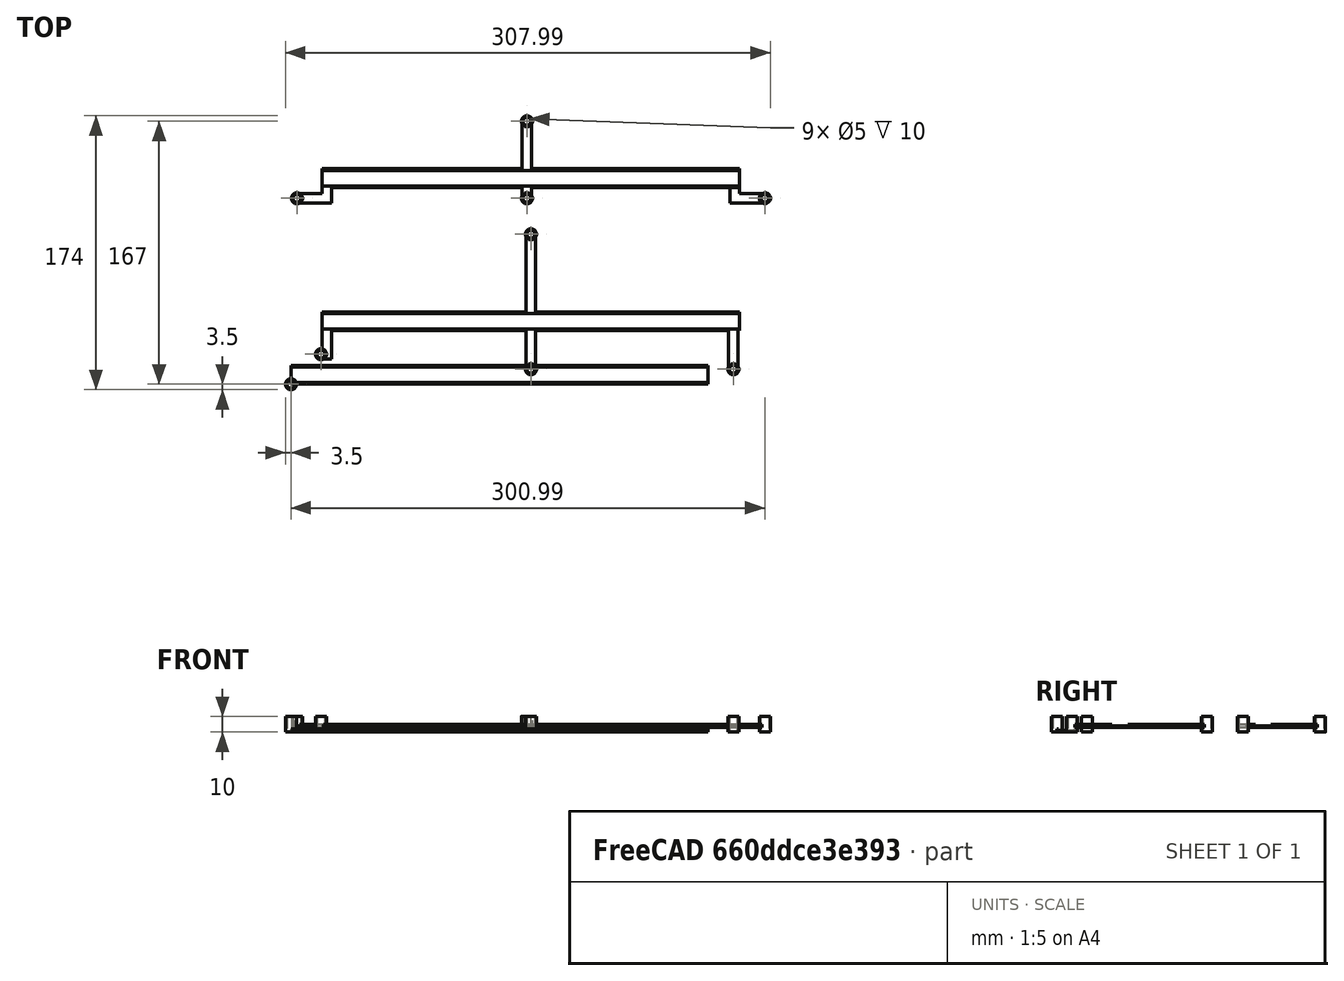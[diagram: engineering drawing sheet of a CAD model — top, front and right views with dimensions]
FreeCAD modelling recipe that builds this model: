
FCSTD DOCUMENT  (FreeCAD 0.18R4 (GitTag))
Label: underglow spacer
License: All rights reserved
LicenseURL: http://en.wikipedia.org/wiki/All_rights_reserved
objects: Part::Extrusion×18, Part::Part2DObjectPython×12, Part::FeaturePython×7, Part::MultiFuse×7, App::DocumentObjectGroup×6, Sketcher::SketchObject×1, Mesh::Feature×1, Part::Mirroring×1
note: 46 computed .brp shape members not serialized (recipe doc carries the construction recipe); baked Part::Feature solids carry a one-line shape summary decoded from their .brp

FEATURE [Sketcher::SketchObject] Sketch  label="donut"
  sketch-geometry (2):
    g0: Circle CenterX=0 CenterY=0 CenterZ=0 NormalX=0 NormalY=0 NormalZ=1 AngleXU=0 Radius=2.5
    g1: Circle CenterX=0 CenterY=0 CenterZ=0 NormalX=0 NormalY=0 NormalZ=1 AngleXU=0 Radius=3.5
  constraints (4):
    c: Coincident(g0,g-1)  'inner_origin'
    c: Radius(g0) = 2.5  'inner_rad'
    c: Coincident(g1,g0)  'outer_origin'
    c: Radius(g1) = 3.5  'outer_rad'
FEATURE [Part::Extrusion] Extrude  label="base_spacer"
  Base = -> Sketch
  Dir = (0,0,1)
  DirMode = 2
  FaceMakerClass = Part::FaceMakerBullseye
  LengthFwd = 10
  LengthRev = 0
  Solid = true
  Symmetric = false
FEATURE [Mesh::Feature] plate
  Placement = pos=(304.8,0,0) rot=(0,1,0;3.14159rad)
FEATURE [App::DocumentObjectGroup] Group  label="REF"
  Group = -> [plate]
FEATURE [App::DocumentObjectGroup] Group001  label="spacer"
  Group = -> [Extrude]
FEATURE [Part::Extrusion] Extrude004  label="t_spacer_top_middle"
  Base = -> Sketch
  Dir = (0,0,1)
  DirMode = 2
  FaceMakerClass = Part::FaceMakerBullseye
  LengthFwd = 10
  LengthRev = 0
  Placement = pos=(149.86,167,0) rot=(0,0,1;0rad)
  Solid = true
  Symmetric = false
FEATURE [Part::Part2DObjectPython] Rectangle003  label="t_top_connector"  # Draft 2D object (typed FeaturePython)
  ChamferSize = 0
  Columns = 1
  FilletRadius = 0
  Height = 31.19
  Length = 6
  MakeFace = true
  Placement = pos=(146.86,136.81,3) rot=(0,0,1;0rad)
  Rows = 1
FEATURE [Part::Extrusion] Extrude005  label="t_ext_top_connector"
  Base = -> Rectangle003
  Dir = (0,0,1)
  DirMode = 2
  FaceMakerClass = Part::FaceMakerBullseye
  LengthFwd = 2
  LengthRev = 0
  Solid = false
  Symmetric = false
FEATURE [Part::FeaturePython] Connect  label="t_connect_spacer_top_connector"  # WARN: FeaturePython — macro-defined, semantics opaque (R4)
  Objects = -> [Extrude005,Extrude004]
  Tolerance = 0
FEATURE [Part::Extrusion] Extrude006  label="t_spacer_bottom_middle"
  Base = -> Sketch
  Dir = (0,0,1)
  DirMode = 2
  FaceMakerClass = Part::FaceMakerBullseye
  LengthFwd = 10
  LengthRev = 0
  Placement = pos=(149.86,118.11,0) rot=(0,0,1;0rad)
  Solid = true
  Symmetric = false
FEATURE [Part::Part2DObjectPython] Rectangle004  label="bottom_connector"  # Draft 2D object (typed FeaturePython)
  ChamferSize = 0
  Columns = 1
  FilletRadius = 0
  Height = 6.7
  Length = 6
  MakeFace = true
  Placement = pos=(146.86,118.11,3) rot=(0,0,1;0rad)
  Rows = 1
FEATURE [Part::Extrusion] Extrude007  label="ex_bottom_connector"
  Base = -> Rectangle004
  Dir = (0,0,1)
  DirMode = 2
  FaceMakerClass = Part::FaceMakerBullseye
  LengthFwd = 2
  LengthRev = 0
  Solid = false
  Symmetric = false
FEATURE [Part::FeaturePython] Connect001  label="t_connect_spacer_connector_bot"  # WARN: FeaturePython — macro-defined, semantics opaque (R4)
  Objects = -> [Extrude006,Extrude007]
  Tolerance = 0
FEATURE [Part::Extrusion] Extrude008  label="t_bl_spacer"
  Base = -> Sketch
  Dir = (0,0,1)
  DirMode = 2
  FaceMakerClass = Part::FaceMakerBullseye
  LengthFwd = 10
  LengthRev = 0
  Placement = pos=(3.81,118.11,0) rot=(0,0,1;0rad)
  Solid = true
  Symmetric = false
FEATURE [Part::Part2DObjectPython] Rectangle005  label="t_bl_con_1"  # Draft 2D object (typed FeaturePython)
  ChamferSize = 0
  Columns = 1
  FilletRadius = 0
  Height = 6
  Length = 22.09
  MakeFace = true
  Placement = pos=(3.81,115.11,3) rot=(0,0,1;0rad)
  Rows = 1
FEATURE [Part::Part2DObjectPython] Rectangle006  label="t_bl_con_2"  # Draft 2D object (typed FeaturePython)
  ChamferSize = 0
  Columns = 1
  FilletRadius = 0
  Height = 9.7
  Length = 6
  MakeFace = true
  Placement = pos=(19.9,115.11,3) rot=(0,0,1;0rad)
  Rows = 1
FEATURE [Part::Part2DObjectPython] Fusion003  label="t_bl_con"  # Draft 2D object (typed FeaturePython)
  Base = -> Rectangle005
  ChamferSize = 0
  Closed = false
  End = (25.9,121.11,3)
  FilletRadius = 0
  Length = 0
  MakeFace = true
  Points = (8) [(25.9,124.81,3),(19.9,124.81,3),(19.9,121.11,3),(3.81,121.11,3),(3.81,115.11,3),(19.9,115.11,3),(25.9,115.11,3),(25.9,121.11,3)]
  Start = (25.9,124.81,3)
  Subdivisions = 0
  Tool = -> Rectangle006
FEATURE [Part::Extrusion] Extrude009  label="t_ext_bl_con"
  Base = -> Fusion003
  Dir = (0,0,1)
  DirMode = 2
  FaceMakerClass = Part::FaceMakerBullseye
  LengthFwd = 2
  LengthRev = 0
  Solid = false
  Symmetric = false
FEATURE [Part::FeaturePython] Connect002  label="t_bl_con_spacer"  # WARN: FeaturePython — macro-defined, semantics opaque (R4)
  Objects = -> [Extrude009,Extrude008]
  Tolerance = 0
FEATURE [Part::Mirroring] Part__Mirroring  label="t_br_con_spacer"
  Base = (152.4,119.96,4.99998)
  Normal = (1,0,-1.19209e-07)
  Source = -> Connect002
FEATURE [Part::Part2DObjectPython] Rectangle007  label="d_top"  # Draft 2D object (typed FeaturePython)
  ChamferSize = 0
  Columns = 1
  FilletRadius = 0
  Height = 1
  Length = 265
  MakeFace = true
  Placement = pos=(0,11,1) rot=(0,0,1;0rad)
  Rows = 1
FEATURE [Part::Part2DObjectPython] Rectangle008  label="d_bottom_lip"  # Draft 2D object (typed FeaturePython)
  ChamferSize = 0
  Columns = 1
  FilletRadius = 0
  Height = 1
  Length = 265
  MakeFace = true
  Placement = pos=(0,0,1) rot=(0,0,1;0rad)
  Rows = 1
FEATURE [Part::Part2DObjectPython] Rectangle009  label="d_base"  # Draft 2D object (typed FeaturePython)
  ChamferSize = 0
  Columns = 1
  FilletRadius = 0
  Height = 12
  Length = 265
  MakeFace = true
  Rows = 1
FEATURE [Part::Extrusion] Extrude010  label="h_base"
  Base = -> Rectangle009
  Dir = (0,0,1)
  DirMode = 2
  FaceMakerClass = Part::FaceMakerBullseye
  LengthFwd = 1
  LengthRev = 0
  Solid = false
  Symmetric = false
FEATURE [Part::Extrusion] Extrude011  label="h_bottom_lip"
  Base = -> Rectangle008
  Dir = (0,0,1)
  DirMode = 2
  FaceMakerClass = Part::FaceMakerBullseye
  LengthFwd = 1
  LengthRev = 0
  Solid = false
  Symmetric = false
FEATURE [Part::Extrusion] Extrude012  label="h_top_lip"
  Base = -> Rectangle007
  Dir = (0,0,1)
  DirMode = 2
  FaceMakerClass = Part::FaceMakerBullseye
  LengthFwd = 1
  LengthRev = 0
  Solid = false
  Symmetric = false
FEATURE [Part::MultiFuse] Fusion005  label="h_holder"
  Shapes = -> [Extrude010,Extrude011,Extrude012]
FEATURE [App::DocumentObjectGroup] Group003  label="holder"
  Group = -> [Fusion005]
FEATURE [App::DocumentObjectGroup] Group005  label="parts"
  Group = -> [Group003,Group001]
FEATURE [Part::MultiFuse] Fusion006  label="t_holder"
  Placement = pos=(19.9,124.81,3) rot=(0,0,1;0rad)
  Shapes = -> [Extrude010,Extrude011,Extrude012]
FEATURE [Part::MultiFuse] Fusion001  label="t_base_w_top_connector"
  Shapes = -> [Connect,Fusion006]
FEATURE [Part::MultiFuse] Fusion002  label="t_base_tcs_bmcs"
  Shapes = -> [Connect001,Fusion001]
FEATURE [Part::MultiFuse] Fusion004  label="top_all"
  Shapes = -> [Fusion002,Part__Mirroring,Connect002]
FEATURE [App::DocumentObjectGroup] Group002  label="top"
  Group = -> [Fusion004]
FEATURE [Part::MultiFuse] Fusion007  label="b_holder"
  Placement = pos=(19.9,34,3) rot=(0,0,1;0rad)
  Shapes = -> [Extrude010,Extrude011,Extrude012]
FEATURE [Part::Extrusion] Extrude013  label="b_bm_spacer"
  Base = -> Sketch
  Dir = (0,0,1)
  DirMode = 2
  FaceMakerClass = Part::FaceMakerBullseye
  LengthFwd = 10
  LengthRev = 0
  Placement = pos=(152.4,9.53,0) rot=(0,0,1;0rad)
  Solid = true
  Symmetric = false
FEATURE [Part::Part2DObjectPython] Rectangle  label="b_bm_connector"  # Draft 2D object (typed FeaturePython)
  ChamferSize = 0
  Columns = 1
  FilletRadius = 0
  Height = 24.47
  Length = 6
  MakeFace = true
  Placement = pos=(149.4,9.53,3) rot=(0,0,1;0rad)
  Rows = 1
FEATURE [Part::Extrusion] Extrude014  label="b_bm_connector_ext"
  Base = -> Rectangle
  Dir = (0,0,1)
  DirMode = 2
  FaceMakerClass = Part::FaceMakerBullseye
  LengthFwd = 2
  LengthRev = 0
  Solid = false
  Symmetric = false
FEATURE [Part::FeaturePython] Connect003  label="b_bm_con"  # WARN: FeaturePython — macro-defined, semantics opaque (R4)
  Objects = -> [Extrude013,Extrude014]
  Tolerance = 0
FEATURE [Part::Extrusion] Extrude015  label="b_tm_spacer"
  Base = -> Sketch
  Dir = (0,0,1)
  DirMode = 2
  FaceMakerClass = Part::FaceMakerBullseye
  LengthFwd = 10
  LengthRev = 0
  Placement = pos=(152.4,95.25,0) rot=(0,0,1;0rad)
  Solid = true
  Symmetric = false
FEATURE [Part::Part2DObjectPython] Rectangle010  label="b_tm_connector"  # Draft 2D object (typed FeaturePython)
  ChamferSize = 0
  Columns = 1
  FilletRadius = 0
  Height = 49.25
  Length = 6
  MakeFace = true
  Placement = pos=(149.4,46,3) rot=(0,0,1;0rad)
  Rows = 1
FEATURE [Part::Extrusion] Extrude016  label="b_tm_connector_ext"
  Base = -> Rectangle010
  Dir = (0,0,1)
  DirMode = 2
  FaceMakerClass = Part::FaceMakerBullseye
  LengthFwd = 2
  LengthRev = 0
  Solid = false
  Symmetric = false
FEATURE [Part::FeaturePython] Connect004  label="b_tm_con"  # WARN: FeaturePython — macro-defined, semantics opaque (R4)
  Objects = -> [Extrude015,Extrude016]
  Tolerance = 0
FEATURE [Part::Extrusion] Extrude017  label="b_bl_spacer"
  Base = -> Sketch
  Dir = (0,0,1)
  DirMode = 2
  FaceMakerClass = Part::FaceMakerBullseye
  LengthFwd = 10
  LengthRev = 0
  Placement = pos=(19.05,19.05,0) rot=(0,0,1;0rad)
  Solid = true
  Symmetric = false
FEATURE [Part::Extrusion] Extrude018  label="b_br_spacer"
  Base = -> Sketch
  Dir = (0,0,1)
  DirMode = 2
  FaceMakerClass = Part::FaceMakerBullseye
  LengthFwd = 10
  LengthRev = 0
  Placement = pos=(280.99,9.53,0) rot=(0,0,1;0rad)
  Solid = true
  Symmetric = false
FEATURE [Part::Part2DObjectPython] Rectangle011  label="b_br_connector"  # Draft 2D object (typed FeaturePython)
  ChamferSize = 0
  Columns = 1
  FilletRadius = 0
  Height = 24.47
  Length = 6
  MakeFace = true
  Placement = pos=(277.99,9.53,3) rot=(0,0,1;0rad)
  Rows = 1
FEATURE [Part::Extrusion] Extrude019  label="b_br_connector_ext"
  Base = -> Rectangle011
  Dir = (0,0,1)
  DirMode = 2
  FaceMakerClass = Part::FaceMakerBullseye
  LengthFwd = 2
  LengthRev = 0
  Solid = false
  Symmetric = false
FEATURE [Part::FeaturePython] Connect005  label="b_br_con"  # WARN: FeaturePython — macro-defined, semantics opaque (R4)
  Objects = -> [Extrude018,Extrude019]
  Tolerance = 0
FEATURE [Part::Part2DObjectPython] Rectangle012  label="b_bl_connector"  # Draft 2D object (typed FeaturePython)
  ChamferSize = 0
  Columns = 1
  FilletRadius = 0
  Height = 18
  Length = 6
  MakeFace = true
  Placement = pos=(19.9,16,3) rot=(0,0,1;0rad)
  Rows = 1
FEATURE [Part::Extrusion] Extrude020  label="b_bl_connector_ext"
  Base = -> Rectangle012
  Dir = (0,0,1)
  DirMode = 2
  FaceMakerClass = Part::FaceMakerBullseye
  LengthFwd = 2
  LengthRev = 0
  Solid = false
  Symmetric = false
FEATURE [Part::FeaturePython] Connect006  label="b_bl_con"  # WARN: FeaturePython — macro-defined, semantics opaque (R4)
  Objects = -> [Extrude020,Extrude017]
  Tolerance = 0
FEATURE [Part::MultiFuse] Fusion  label="bottom_all"
  Shapes = -> [Fusion007,Connect004,Connect005,Connect006,Connect003]
FEATURE [App::DocumentObjectGroup] Group004  label="bottom"
  Group = -> [Fusion]
